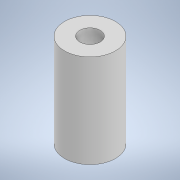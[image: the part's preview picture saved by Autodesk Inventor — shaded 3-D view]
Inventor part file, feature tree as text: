
AUTODESK INVENTOR PART (.ipt)
format: ipt  version: 2021.2 (Build 252289000, 289)  size: 130,048 bytes
history: native  units: mm
features: sketch x4, other x3, extrude x2, hole x2, thread x1
ambient origin geometry x8: Origin, YZ Plane, XZ Plane, XY Plane, X Axis, Y Axis, Z Axis, Center Point
bodies: Body1 (feature_tree)
feature tree (12):
  other  "Твердое тело1"
  extrude  "Выдавливание1"  Depth=30.0mm
  other  "РабПлоскость1"
  hole  "Отверстие2"  [1 undecoded]
  other  "РабПлоскость2"
  hole  "Отверстие3"  [1 undecoded]
  extrude  "Выдавливание2"  Depth=20.0mm TaperAngle=0.0deg
  thread  "Резьба1"
  sketch  "Эскиз1"
  sketch  "Эскиз5"
  sketch  "Эскиз6"
  sketch  "Эскиз7"
note: 2 required parameter values undecoded (feature->parameter linkage not recoverable at this tier; creation-order binding heuristic only, values carry confidence <= 0.55)
